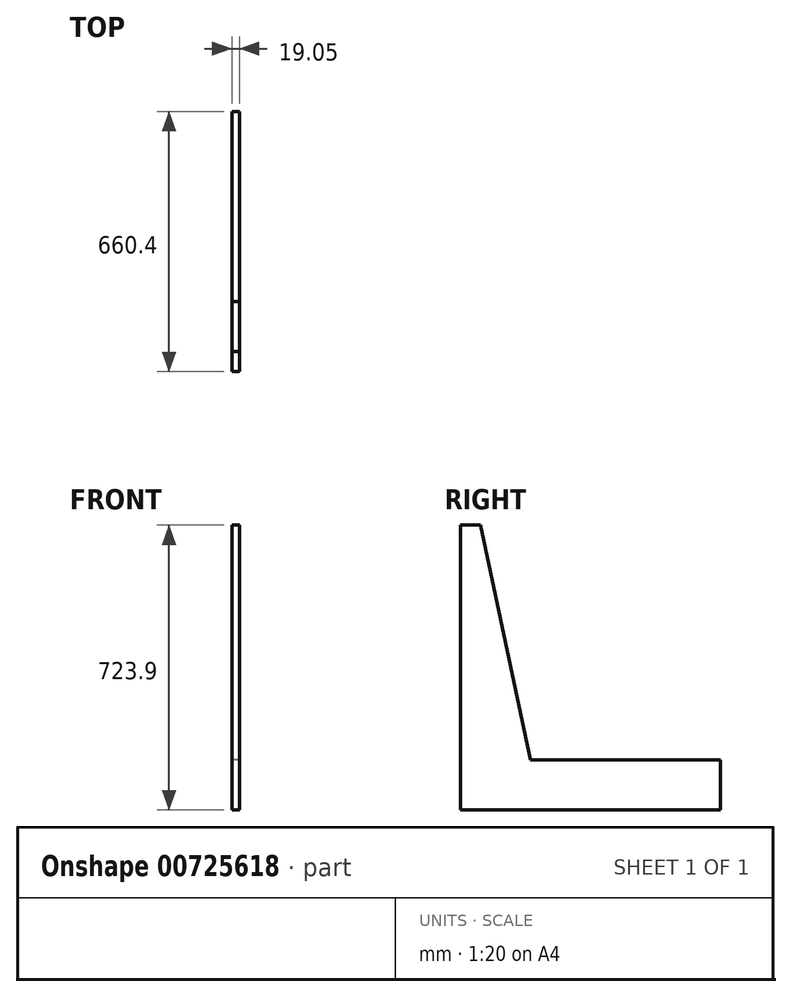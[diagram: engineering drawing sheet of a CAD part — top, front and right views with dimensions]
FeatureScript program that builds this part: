
annotation { "Feature Type Name" : "Feature", "Feature Type Description" : "" }
export const myFeature = defineFeature(function(context is Context, id is Id, definition is map)
    precondition{}
    {
        {
            var Q0;
            Q0=qCreatedBy(makeId("Right.planeOp"),FACE);
            var sketch = newSketch(context, id + "F0", { "sketchPlane" : qUnion([Q0])});
            skLineSegment(sketch, "E0.bottom", {"start": v(-161.8, 213.66) * mm, "end": v(-111, 213.66) * mm});
            skLineSegment(sketch, "E0.top", {"start": v(-161.8, -510.24) * mm, "end": v(498.6, -510.24) * mm});
            skLineSegment(sketch, "E0.left", {"start": v(-161.8, 213.66) * mm, "end": v(-161.8, -510.24) * mm});
            skLineSegment(sketch, "E1", {"start": v(498.6, -383.24) * mm, "end": v(16, -383.24) * mm});
            skLineSegment(sketch, "E2", {"start": v(16, -383.24) * mm, "end": v(-111, 213.66) * mm});
            skLineSegment(sketch, "E3", {"start": v(498.6, -383.24) * mm, "end": v(498.6, -510.24) * mm});
            skSolve(sketch);
        }
        {
            var Q0;
            Q0=makeQuery(id+"F0.imprint","IMPRINT",FACE,{"disambiguationData":[TD([[makeQuery(id+"F0.imprint","IMPRINT",EDGE,{"derivedFrom":sQuery(id+"F0.wireOp",EDGE,"E0.top")}),1.0]])]});
            extrude(context, id + "F1", {"entities" : qUnion([Q0]), "depth" : 19.05 * mm, "offsetDistance" : 25.4 * mm});
        }
    });
